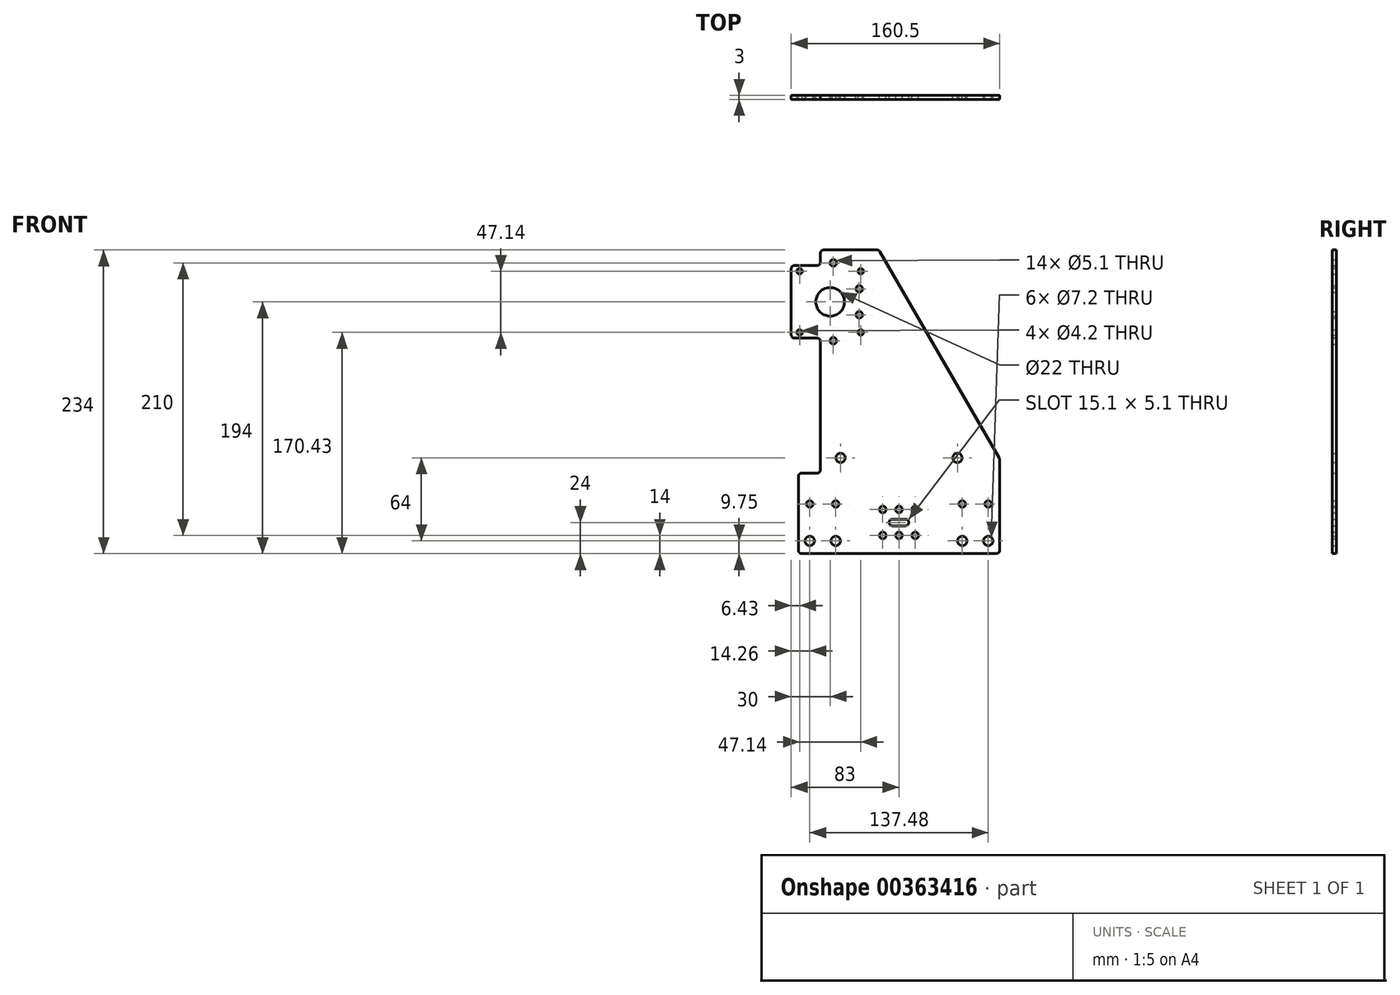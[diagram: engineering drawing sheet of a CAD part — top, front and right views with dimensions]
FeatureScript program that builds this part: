
annotation { "Feature Type Name" : "Feature", "Feature Type Description" : "" }
export const myFeature = defineFeature(function(context is Context, id is Id, definition is map)
    precondition{}
    {
        {
            var Q0;
            Q0=qCreatedBy(makeId("Front.planeOp"),FACE);
            var sketch = newSketch(context, id + "F0", { "sketchPlane" : qUnion([Q0])});
            skLineSegment(sketch, "E0", {"start": v(-60.5, 207.5) * mm, "end": v(-60.5, 200.5) * mm});
            skLineSegment(sketch, "E1", {"start": v(77.5, -21.5) * mm, "end": v(77.5, 48.33) * mm});
            skLineSegment(sketch, "E2", {"start": v(-16.94, 210) * mm, "end": v(-58, 210) * mm});
            skPoint(sketch, "E3", {"position": v(-68.74, -14.25) * mm});
            skPoint(sketch, "E4", {"position": v(-48.74, -14.25) * mm});
            skPoint(sketch, "E5", {"position": v(48.74, -14.25) * mm});
            skPoint(sketch, "E6", {"position": v(68.74, -14.25) * mm});
            skPoint(sketch, "E7", {"position": v(68.74, 14.25) * mm});
            skPoint(sketch, "E8", {"position": v(48.74, 14.25) * mm});
            skPoint(sketch, "E9", {"position": v(-48.74, 14.25) * mm});
            skPoint(sketch, "E10", {"position": v(-68.74, 14.25) * mm});
            skPoint(sketch, "E11", {"position": v(-45, 49.75) * mm});
            skPoint(sketch, "E12", {"position": v(45, 49.75) * mm});
            skLineSegment(sketch, "E13", {"start": v(-63, 38) * mm, "end": v(-75, 38) * mm});
            skLineSegment(sketch, "E14", {"start": v(-77.5, 35.5) * mm, "end": v(-77.5, -21.5) * mm});
            skLineSegment(sketch, "E15", {"start": v(-63, 198) * mm, "end": v(-80.5, 198) * mm});
            skLineSegment(sketch, "E16", {"start": v(-83, 195.5) * mm, "end": v(-83, 144.5) * mm});
            skLineSegment(sketch, "E17", {"start": v(-80.5, 142) * mm, "end": v(-63, 142) * mm});
            skPoint(sketch, "E17.endSnap0", {"position": v(-60.5, 124) * mm});
            skLineSegment(sketch, "E18.trimOffspring", {"start": v(-60.5, 139.5) * mm, "end": v(-60.5, 40.5) * mm});
            skLineSegment(sketch, "E19", {"start": v(-75, -24) * mm, "end": v(75, -24) * mm});
            skLineSegment(sketch, "E20", {"start": v(-14.78, 208.75) * mm, "end": v(77.16, 49.58) * mm});
            skPoint(sketch, "E21", {"position": v(-12.5, 10) * mm});
            skPoint(sketch, "E22", {"position": v(0, 10) * mm});
            skPoint(sketch, "E23", {"position": v(12.5, 10) * mm});
            skPoint(sketch, "E24", {"position": v(12.5, -10) * mm});
            skPoint(sketch, "E25", {"position": v(0, -10) * mm});
            skPoint(sketch, "E26", {"position": v(-12.5, -10) * mm});
            skPoint(sketch, "E27", {"position": v(-5, 0) * mm});
            skPoint(sketch, "E28", {"position": v(5, 0) * mm});
            skPoint(sketch, "E29", {"position": v(-76.57, 193.57) * mm});
            skPoint(sketch, "E30", {"position": v(-76.57, 146.43) * mm});
            skPoint(sketch, "E31", {"position": v(-29.43, 146.43) * mm});
            skPoint(sketch, "E32", {"position": v(-29.43, 193.57) * mm});
            skPoint(sketch, "E33", {"position": v(-30.6, 180) * mm});
            skPoint(sketch, "E34", {"position": v(-30.6, 160) * mm});
            skPoint(sketch, "E35", {"position": v(-53, 170) * mm});
            skPoint(sketch, "E36", {"position": v(-50.6, 200) * mm});
            skPoint(sketch, "E37", {"position": v(-50.6, 140) * mm});
            skLineSegment(sketch, "E38", {"start": v(-83, 170) * mm, "end": v(-0.5, 170) * mm, "construction": true});
            skPoint(sketch, "E39", {"position": v(0, -24) * mm});
            skLineSegment(sketch, "E40", {"start": v(0, -24) * mm, "end": v(0, 206) * mm, "construction": true});
            skLineSegment(sketch, "E41", {"start": v(-88.98, 0) * mm, "end": v(88.44, 0) * mm, "construction": true});
            skPoint(sketch, "E42.visualSharp", {"position": v(-60.5, 210) * mm});
            skArc(sketch, "E42.filletArc", {"start": v(-58, 210) * mm, "mid": v(-59.77, 209.27) * mm, "end": v(-60.5, 207.5) * mm});
            skPoint(sketch, "E43.visualSharp", {"position": v(-15.5, 210) * mm});
            skArc(sketch, "E43.filletArc", {"start": v(-14.78, 208.75) * mm, "mid": v(-15.7, 209.67) * mm, "end": v(-16.94, 210) * mm});
            skPoint(sketch, "E44.visualSharp", {"position": v(-60.5, 198) * mm});
            skArc(sketch, "E44.filletArc", {"start": v(-63, 198) * mm, "mid": v(-61.23, 198.73) * mm, "end": v(-60.5, 200.5) * mm});
            skPoint(sketch, "E45.visualSharp", {"position": v(-83, 198) * mm});
            skArc(sketch, "E45.filletArc", {"start": v(-80.5, 198) * mm, "mid": v(-82.27, 197.27) * mm, "end": v(-83, 195.5) * mm});
            skPoint(sketch, "E46.visualSharp", {"position": v(-83, 142) * mm});
            skArc(sketch, "E46.filletArc", {"start": v(-83, 144.5) * mm, "mid": v(-82.27, 142.73) * mm, "end": v(-80.5, 142) * mm});
            skPoint(sketch, "E47.visualSharp", {"position": v(-60.5, 142) * mm});
            skArc(sketch, "E47.filletArc", {"start": v(-60.5, 139.5) * mm, "mid": v(-61.23, 141.27) * mm, "end": v(-63, 142) * mm});
            skPoint(sketch, "E48.visualSharp", {"position": v(77.5, -24) * mm});
            skArc(sketch, "E48.filletArc", {"start": v(75, -24) * mm, "mid": v(76.77, -23.27) * mm, "end": v(77.5, -21.5) * mm});
            skPoint(sketch, "E49.visualSharp", {"position": v(-77.5, -24) * mm});
            skArc(sketch, "E49.filletArc", {"start": v(-77.5, -21.5) * mm, "mid": v(-76.77, -23.27) * mm, "end": v(-75, -24) * mm});
            skPoint(sketch, "E50.visualSharp", {"position": v(-77.5, 38) * mm});
            skArc(sketch, "E50.filletArc", {"start": v(-75, 38) * mm, "mid": v(-76.77, 37.27) * mm, "end": v(-77.5, 35.5) * mm});
            skPoint(sketch, "E51.visualSharp", {"position": v(-60.5, 38) * mm});
            skArc(sketch, "E51.filletArc", {"start": v(-63, 38) * mm, "mid": v(-61.23, 38.73) * mm, "end": v(-60.5, 40.5) * mm});
            skPoint(sketch, "E52.visualSharp", {"position": v(77.5, 49) * mm});
            skArc(sketch, "E52.filletArc", {"start": v(77.5, 48.33) * mm, "mid": v(77.41, 48.98) * mm, "end": v(77.16, 49.58) * mm});
            skLineSegment(sketch, "E53.bottom", {"start": v(-5, 2.55) * mm, "end": v(5, 2.55) * mm});
            skLineSegment(sketch, "E53.top", {"start": v(-5, -2.55) * mm, "end": v(5, -2.55) * mm});
            skLineSegment(sketch, "E53.left", {"start": v(-5, 2.55) * mm, "end": v(-5, -2.55) * mm});
            skLineSegment(sketch, "E53.right", {"start": v(5, 2.55) * mm, "end": v(5, -2.55) * mm});
            skPoint(sketch, "E53.middle", {"position": v(0, 0) * mm});
            skSolve(sketch);
        }
        {
            var Q0;
            Q0=makeQuery(id+"F0.imprint","IMPRINT",FACE,{"disambiguationData":[TD([[makeQuery(id+"F0.imprint","IMPRINT",EDGE,{"derivedFrom":sQuery(id+"F0.wireOp",EDGE,"E0")}),1.0]])]});
            extrude(context, id + "F1", {"entities" : qUnion([Q0]), "depth" : 3 * mm, "offsetDistance" : 25 * mm});
        }
        {
            var Q0;
            Q0=sQuery(id+"F0.wireOp",VERTEX,"E35");
            var Q1;
            Q1=makeQuery(id+"F1.opExtrude","SWEPT_BODY",BODY,{"disambiguationData":[OSD([sQuery(id+"F0.wireOp",EDGE,"E0"),sQuery(id+"F0.wireOp",EDGE,"E1"),sQuery(id+"F0.wireOp",EDGE,"E2"),sQuery(id+"F0.wireOp",EDGE,"E13"),sQuery(id+"F0.wireOp",EDGE,"E14"),sQuery(id+"F0.wireOp",EDGE,"E15"),sQuery(id+"F0.wireOp",EDGE,"E16"),sQuery(id+"F0.wireOp",EDGE,"E17"),sQuery(id+"F0.wireOp",EDGE,"E18.trimOffspring"),sQuery(id+"F0.wireOp",EDGE,"E19"),sQuery(id+"F0.wireOp",EDGE,"E20")])]});
            hole(context, id + "F2", {"style" : HoleStyle.SIMPLE, "endStyle" : HoleEndStyle.THROUGH, "oppositeDirection" : true, "standardTappedOrClearance" : lookupTablePath({ "standard" : "ISO", "size" : "22", "type" : "Drilled" }), "standardBlindInLast" : lookupTablePath({ "standard" : "ISO", "size" : "22", "type" : "Drilled" }), "holeDiameter" : 22 * mm, "isTappedThrough" : true, "tappedDepth" : 7.5 * mm, "tapClearance" : 3, "startFromSketch" : true, "locations" : qUnion([Q0]), "scope" : qUnion([Q1])});
        }
        {
            var Q0;
            Q0=sQuery(id+"F0.wireOp",VERTEX,"E29");
            var Q1;
            Q1=sQuery(id+"F0.wireOp",VERTEX,"E32");
            var Q2;
            Q2=sQuery(id+"F0.wireOp",VERTEX,"E31");
            var Q3;
            Q3=sQuery(id+"F0.wireOp",VERTEX,"E30");
            var Q4;
            Q4=makeQuery(id+"F1.opExtrude","SWEPT_BODY",BODY,{"disambiguationData":[OSD([sQuery(id+"F0.wireOp",EDGE,"E0"),sQuery(id+"F0.wireOp",EDGE,"E1"),sQuery(id+"F0.wireOp",EDGE,"E2"),sQuery(id+"F0.wireOp",EDGE,"E13"),sQuery(id+"F0.wireOp",EDGE,"E14"),sQuery(id+"F0.wireOp",EDGE,"E15"),sQuery(id+"F0.wireOp",EDGE,"E16"),sQuery(id+"F0.wireOp",EDGE,"E17"),sQuery(id+"F0.wireOp",EDGE,"E18.trimOffspring"),sQuery(id+"F0.wireOp",EDGE,"E19"),sQuery(id+"F0.wireOp",EDGE,"E20")])]});
            hole(context, id + "F3", {"style" : HoleStyle.SIMPLE, "endStyle" : HoleEndStyle.THROUGH, "oppositeDirection" : true, "standardTappedOrClearance" : lookupTablePath({ "standard" : "ISO", "engagement" : "75%", "pitch" : "0.8 mm", "size" : "M5", "type" : "Tapped" }), "standardBlindInLast" : lookupTablePath({ "standard" : "ISO", "engagement" : "75%", "pitch" : "0.8 mm", "size" : "M5", "type" : "Tapped" }), "holeDiameter" : 4.2 * mm, "showTappedDepth" : true, "isTappedThrough" : true, "tappedDepth" : 7.5 * mm, "tapClearance" : 3, "startFromSketch" : true, "locations" : qUnion([Q0, Q1, Q2, Q3]), "scope" : qUnion([Q4]), "majorDiameter" : 5 * mm});
        }
        {
            var Q0;
            Q0=sQuery(id+"F0.wireOp",VERTEX,"E36");
            var Q1;
            Q1=sQuery(id+"F0.wireOp",VERTEX,"E33");
            var Q2;
            Q2=sQuery(id+"F0.wireOp",VERTEX,"E34");
            var Q3;
            Q3=sQuery(id+"F0.wireOp",VERTEX,"E37");
            var Q4;
            Q4=sQuery(id+"F0.wireOp",VERTEX,"E10");
            var Q5;
            Q5=sQuery(id+"F0.wireOp",VERTEX,"E9");
            var Q6;
            Q6=sQuery(id+"F0.wireOp",VERTEX,"E8");
            var Q7;
            Q7=sQuery(id+"F0.wireOp",VERTEX,"E7");
            var Q8;
            Q8=sQuery(id+"F0.wireOp",VERTEX,"E23");
            var Q9;
            Q9=sQuery(id+"F0.wireOp",VERTEX,"E22");
            var Q10;
            Q10=sQuery(id+"F0.wireOp",VERTEX,"E21");
            var Q11;
            Q11=sQuery(id+"F0.wireOp",VERTEX,"E26");
            var Q12;
            Q12=sQuery(id+"F0.wireOp",VERTEX,"E25");
            var Q13;
            Q13=sQuery(id+"F0.wireOp",VERTEX,"E24");
            var Q14;
            Q14=sQuery(id+"F0.wireOp",VERTEX,"E28");
            var Q15;
            Q15=sQuery(id+"F0.wireOp",VERTEX,"E27");
            var Q16;
            Q16=makeQuery(id+"F1.opExtrude","SWEPT_BODY",BODY,{"disambiguationData":[OSD([sQuery(id+"F0.wireOp",EDGE,"E0"),sQuery(id+"F0.wireOp",EDGE,"E1"),sQuery(id+"F0.wireOp",EDGE,"E2"),sQuery(id+"F0.wireOp",EDGE,"E13"),sQuery(id+"F0.wireOp",EDGE,"E14"),sQuery(id+"F0.wireOp",EDGE,"E15"),sQuery(id+"F0.wireOp",EDGE,"E16"),sQuery(id+"F0.wireOp",EDGE,"E17"),sQuery(id+"F0.wireOp",EDGE,"E18.trimOffspring"),sQuery(id+"F0.wireOp",EDGE,"E19"),sQuery(id+"F0.wireOp",EDGE,"E20")])]});
            hole(context, id + "F4", {"style" : HoleStyle.SIMPLE, "endStyle" : HoleEndStyle.THROUGH, "oppositeDirection" : true, "standardTappedOrClearance" : lookupTablePath({ "standard" : "ISO", "size" : "5.1", "type" : "Drilled" }), "standardBlindInLast" : lookupTablePath({ "standard" : "ISO", "size" : "5.1", "type" : "Drilled" }), "holeDiameter" : 5.1 * mm, "isTappedThrough" : true, "tappedDepth" : 7.5 * mm, "tapClearance" : 3, "startFromSketch" : true, "locations" : qUnion([Q0, Q1, Q2, Q3, Q4, Q5, Q6, Q7, Q8, Q9, Q10, Q11, Q12, Q13, Q14, Q15]), "scope" : qUnion([Q16])});
        }
        {
            var Q0;
            Q0=sQuery(id+"F0.wireOp",VERTEX,"E3");
            var Q1;
            Q1=sQuery(id+"F0.wireOp",VERTEX,"E4");
            var Q2;
            Q2=sQuery(id+"F0.wireOp",VERTEX,"E5");
            var Q3;
            Q3=sQuery(id+"F0.wireOp",VERTEX,"E6");
            var Q4;
            Q4=sQuery(id+"F0.wireOp",VERTEX,"E11");
            var Q5;
            Q5=sQuery(id+"F0.wireOp",VERTEX,"E12");
            var Q6;
            Q6=makeQuery(id+"F1.opExtrude","SWEPT_BODY",BODY,{"disambiguationData":[OSD([sQuery(id+"F0.wireOp",EDGE,"E0"),sQuery(id+"F0.wireOp",EDGE,"E1"),sQuery(id+"F0.wireOp",EDGE,"E2"),sQuery(id+"F0.wireOp",EDGE,"E13"),sQuery(id+"F0.wireOp",EDGE,"E14"),sQuery(id+"F0.wireOp",EDGE,"E15"),sQuery(id+"F0.wireOp",EDGE,"E16"),sQuery(id+"F0.wireOp",EDGE,"E17"),sQuery(id+"F0.wireOp",EDGE,"E18.trimOffspring"),sQuery(id+"F0.wireOp",EDGE,"E19"),sQuery(id+"F0.wireOp",EDGE,"E20")])]});
            hole(context, id + "F5", {"style" : HoleStyle.SIMPLE, "endStyle" : HoleEndStyle.THROUGH, "oppositeDirection" : true, "standardTappedOrClearance" : lookupTablePath({ "standard" : "ISO", "size" : "7.2", "type" : "Drilled" }), "standardBlindInLast" : lookupTablePath({ "standard" : "ISO", "size" : "7.2", "type" : "Drilled" }), "holeDiameter" : 7.2 * mm, "isTappedThrough" : true, "tappedDepth" : 7.5 * mm, "tapClearance" : 3, "startFromSketch" : true, "locations" : qUnion([Q0, Q1, Q2, Q3, Q4, Q5]), "scope" : qUnion([Q6])});
        }
    });
